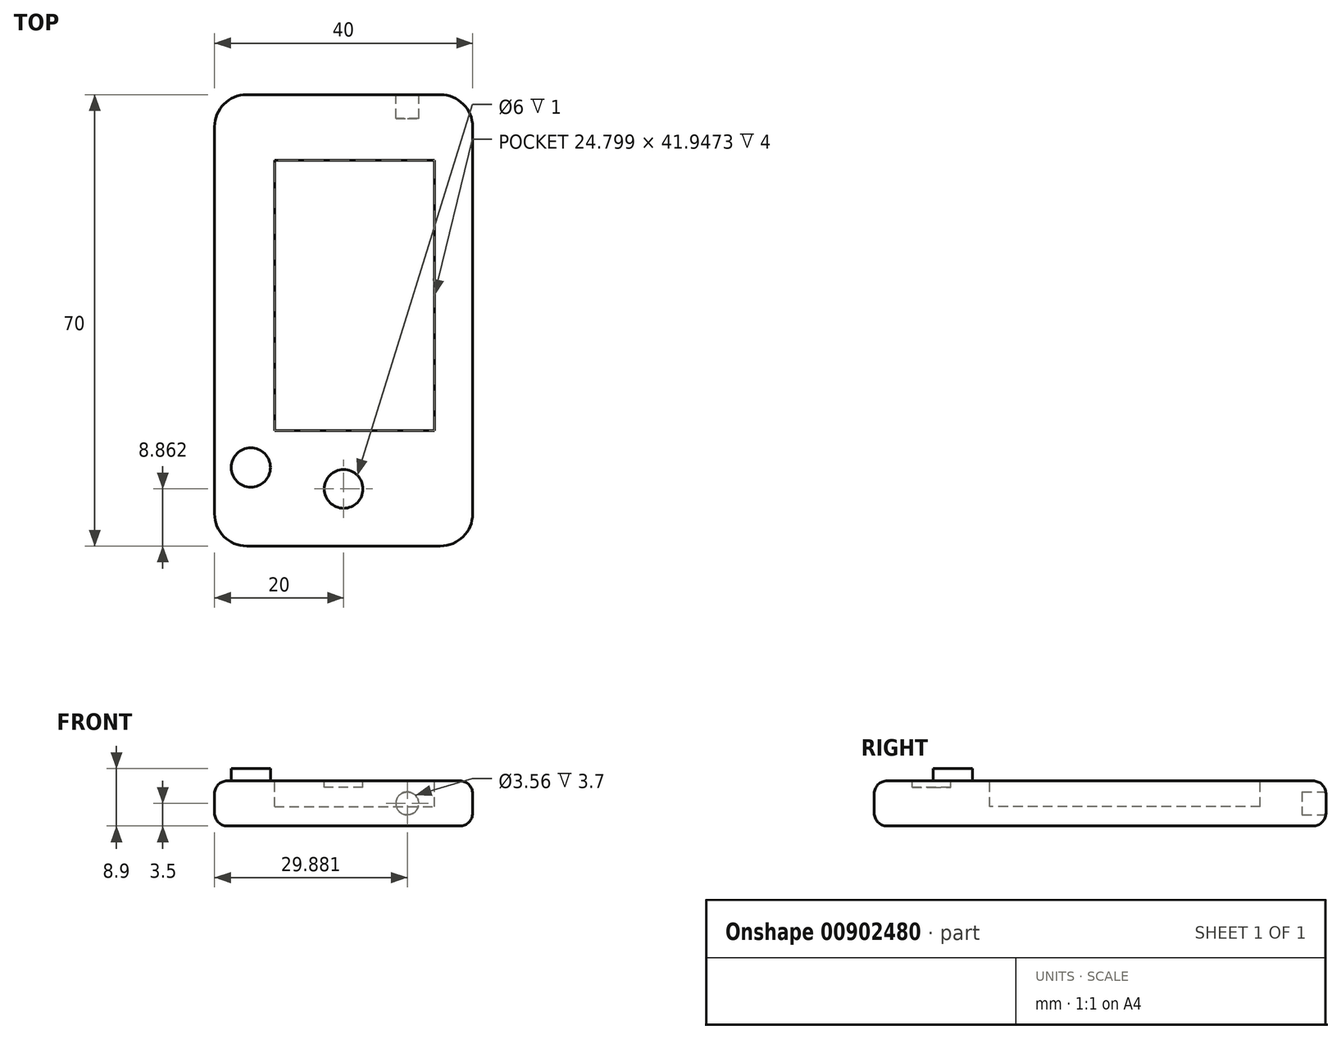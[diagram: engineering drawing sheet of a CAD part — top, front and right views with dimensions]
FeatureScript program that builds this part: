
annotation { "Feature Type Name" : "Feature", "Feature Type Description" : "" }
export const myFeature = defineFeature(function(context is Context, id is Id, definition is map)
    precondition{}
    {
        {
            var Q0;
            Q0=qCreatedBy(makeId("Top.planeOp"),FACE);
            var sketch = newSketch(context, id + "F0", { "sketchPlane" : qUnion([Q0])});
            skLineSegment(sketch, "E0.bottom", {"start": v(0, 0) * mm, "end": v(40, 0) * mm});
            skLineSegment(sketch, "E0.top", {"start": v(0, 70) * mm, "end": v(40, 70) * mm});
            skLineSegment(sketch, "E0.left", {"start": v(0, 0) * mm, "end": v(0, 70) * mm});
            skLineSegment(sketch, "E0.right", {"start": v(40, 0) * mm, "end": v(40, 70) * mm});
            skSolve(sketch);
        }
        {
            var Q0;
            Q0=makeQuery(id+"F0.imprint","IMPRINT",FACE,{"disambiguationData":[TD([[makeQuery(id+"F0.imprint","IMPRINT",EDGE,{"derivedFrom":sQuery(id+"F0.wireOp",EDGE,"E0.bottom")}),1.0]])]});
            extrude(context, id + "F1", {"entities" : qUnion([Q0]), "depth" : 7 * mm, "offsetDistance" : 25 * mm});
        }
        {
            var Q0;
            Q0=makeQuery(id+"F1.opExtrude","SWEPT_EDGE",EDGE,{"disambiguationData":[OSD([sQuery(id+"F0.wireOp",EDGE,"E0.bottom"),sQuery(id+"F0.wireOp",EDGE,"E0.left")])]});
            var Q1;
            Q1=makeQuery(id+"F1.opExtrude","SWEPT_EDGE",EDGE,{"disambiguationData":[OSD([sQuery(id+"F0.wireOp",EDGE,"E0.bottom"),sQuery(id+"F0.wireOp",EDGE,"E0.right")])]});
            var Q2;
            Q2=makeQuery(id+"F1.opExtrude","SWEPT_EDGE",EDGE,{"disambiguationData":[OSD([sQuery(id+"F0.wireOp",EDGE,"E0.top"),sQuery(id+"F0.wireOp",EDGE,"E0.right")])]});
            var Q3;
            Q3=makeQuery(id+"F1.opExtrude","SWEPT_EDGE",EDGE,{"disambiguationData":[OSD([sQuery(id+"F0.wireOp",EDGE,"E0.top"),sQuery(id+"F0.wireOp",EDGE,"E0.left")])]});
            fillet(context, id + "F2", {"entities" : qUnion([Q0, Q1, Q2, Q3]), "radius" : 5 * mm, "tangentPropagation" : true, "allowEdgeOverflow" : false});
        }
        {
            var Q0;
            Q0=makeQuery(id+"F1.opExtrude","SWEPT_FACE",FACE,{"disambiguationData":[OSD([sQuery(id+"F0.wireOp",EDGE,"E0.top")])]});
            var sketch = newSketch(context, id + "F3", { "sketchPlane" : qUnion([Q0])});
            skCircle(sketch, "E1", {"center": v(-29.88, 3.5) * mm, "radius": 1.78 * mm});
            skPoint(sketch, "E1.centerSnap0", {"position": v(-35, 3.5) * mm});
            skSolve(sketch);
        }
        {
            var Q0;
            Q0=makeQuery(id+"F3.imprint","IMPRINT",FACE,{"disambiguationData":[TD([[makeQuery(id+"F3.imprint","IMPRINT",EDGE,{"derivedFrom":sQuery(id+"F3.wireOp",EDGE,"E1")}),1.0]])]});
            extrude(context, id + "F4", {"entities" : qUnion([Q0]), "operationType" : NewBodyOperationType.REMOVE, "oppositeDirection" : true, "depth" : 3.7 * mm, "offsetDistance" : 25 * mm});
        }
        {
            var Q0;
            Q0=makeQuery(id+"F1.opExtrude","CAP_EDGE",EDGE,{"disambiguationData":[OSD([sQuery(id+"F0.wireOp",EDGE,"E0.right")])],"isStart":true});
            var Q1;
            Q1=makeQuery(id+"F1.opExtrude","CAP_EDGE",EDGE,{"disambiguationData":[OSD([sQuery(id+"F0.wireOp",EDGE,"E0.right")])],"isStart":false});
            fillet(context, id + "F5", {"entities" : qUnion([Q0, Q1]), "radius" : 2 * mm, "tangentPropagation" : true, "allowEdgeOverflow" : false});
        }
        {
            var Q0;
            Q0=makeQuery(id+"F1.opExtrude","CAP_FACE",FACE,{"disambiguationData":[OSD([sQuery(id+"F0.wireOp",EDGE,"E0.bottom"),sQuery(id+"F0.wireOp",EDGE,"E0.top"),sQuery(id+"F0.wireOp",EDGE,"E0.left"),sQuery(id+"F0.wireOp",EDGE,"E0.right")])],"isStart":false});
            var sketch = newSketch(context, id + "F6", { "sketchPlane" : qUnion([Q0])});
            skCircle(sketch, "E2", {"center": v(20, 8.86) * mm, "radius": 3 * mm});
            skPoint(sketch, "E2.centerSnap0", {"position": v(20, 2) * mm});
            skSolve(sketch);
        }
        {
            var Q0;
            Q0=makeQuery(id+"F6.imprint","IMPRINT",FACE,{"disambiguationData":[TD([[makeQuery(id+"F6.imprint","IMPRINT",EDGE,{"derivedFrom":sQuery(id+"F6.wireOp",EDGE,"E2")}),1.0]])]});
            extrude(context, id + "F7", {"entities" : qUnion([Q0]), "operationType" : NewBodyOperationType.REMOVE, "oppositeDirection" : true, "depth" : 1 * mm, "offsetDistance" : 25 * mm});
        }
        {
            var Q0;
            Q0=makeQuery(id+"F1.opExtrude","CAP_FACE",FACE,{"disambiguationData":[OSD([sQuery(id+"F0.wireOp",EDGE,"E0.bottom"),sQuery(id+"F0.wireOp",EDGE,"E0.top"),sQuery(id+"F0.wireOp",EDGE,"E0.left"),sQuery(id+"F0.wireOp",EDGE,"E0.right")])],"isStart":false});
            var sketch = newSketch(context, id + "F8", { "sketchPlane" : qUnion([Q0])});
            skLineSegment(sketch, "E3.bottom", {"start": v(9.3, 59.82) * mm, "end": v(34.1, 59.82) * mm});
            skLineSegment(sketch, "E3.top", {"start": v(9.3, 17.87) * mm, "end": v(34.1, 17.87) * mm});
            skLineSegment(sketch, "E3.left", {"start": v(9.3, 59.82) * mm, "end": v(9.3, 17.87) * mm});
            skLineSegment(sketch, "E3.right", {"start": v(34.1, 59.82) * mm, "end": v(34.1, 17.87) * mm});
            skSolve(sketch);
        }
        {
            var Q0;
            Q0 = qSketchRegion(id + "F8", true);
            extrude(context, id + "F9", {"entities" : qUnion([Q0]), "operationType" : NewBodyOperationType.REMOVE, "oppositeDirection" : true, "depth" : 4 * mm, "offsetDistance" : 25 * mm});
        }
        {
            var Q0;
            Q0=makeQuery(id+"F1.opExtrude","CAP_FACE",FACE,{"disambiguationData":[OSD([sQuery(id+"F0.wireOp",EDGE,"E0.bottom"),sQuery(id+"F0.wireOp",EDGE,"E0.top"),sQuery(id+"F0.wireOp",EDGE,"E0.left"),sQuery(id+"F0.wireOp",EDGE,"E0.right")])],"isStart":false});
            var sketch = newSketch(context, id + "F10", { "sketchPlane" : qUnion([Q0])});
            skCircle(sketch, "E4", {"center": v(5.62, 12.19) * mm, "radius": 3.04 * mm});
            skSolve(sketch);
        }
        {
            var Q0;
            Q0=makeQuery(id+"F10.imprint","IMPRINT",FACE,{"disambiguationData":[TD([[makeQuery(id+"F10.imprint","IMPRINT",EDGE,{"derivedFrom":sQuery(id+"F10.wireOp",EDGE,"E4")}),1.0]])]});
            extrude(context, id + "F11", {"entities" : qUnion([Q0]), "operationType" : NewBodyOperationType.ADD, "depth" : 1.9 * mm, "offsetDistance" : 25 * mm});
        }
    });
